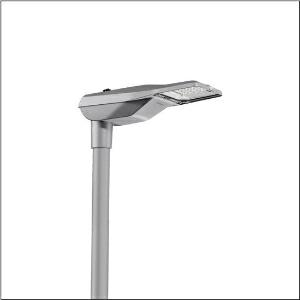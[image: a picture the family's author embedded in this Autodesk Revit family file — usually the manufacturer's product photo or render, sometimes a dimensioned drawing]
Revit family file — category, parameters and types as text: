
# Revit family: streetlight_sl_21_iq_micro___st1_0ab_5xe1m31v08cb_08ed
name_source: partatom
category: Lighting Fixtures
units: mm (PartAtom-declared; Revit-internal decimal feet)

## family parameters
Cut with Voids When Loaded = No
Host = Face
Light Source = No
Part Type = Normal
Room Calculation Point = No
Round Connector Dimension = Use Diameter
Shared = No

## types (1)
- --- (1 x LED, 2530 lm, 19.1 W, 3000K)
    Apparent Load = 19 VA
    CIE Flux Codes = 38 73 97 100 100
    Color Rendering = 70
    Color Temperature = 3000K
    Default Elevation = 1800 mm
    Description = Streetlight SL 21 iQ micro, mast luminaire, primary light control with lens, of PMMA, primary optical cover: cover, of toughened safety glass, transparent, light distribution: ST1.0aB, light emission: direct distribution, primary light characteristic: asymmetric, installation type: post-top, side-entry, LED, High Power LED, rated luminous flux: 2.530lm, luminous efficacy: 133lm/W, light colour: 730, colour temperature: 3000K, control: presetting dimming logarithmic, Street-Remote, Auto-Match, Temp-Guard, Lumen-Switch, Night-Set, Smart-Wire, Light-Fading, Desk-Remote (wireless, voltage-free reading and setting of iQ features in the workshop via application-optimized NFC function/RFID function), optimised constant luminous flux control (CLO 2.0), mains connection: 220..240V, AC, 50/60Hz, start of lifetime: 19W, end of service life: 20W, reduction: 9W, luminaire housing, of diecast aluminium, powder-coated, Siteco® metallic grey (DB 702S), corrosivity category C5 mid according to DIN EN ISO 12944, please order mast flange separately, inclination adjustable: 0°, 5°, 10°, 15°, sealing non-destructively replaceable, multi-level sealing system, length: 528mm, width: 235mm, height: 110mm, mast flange for spigot size: 42mm (side-entry): 5XC10008XM4, 60/48mm (side-entry/post-top): 5XC10108XM2, 76/60mm (side-entry/post-top): 5XC10108XM1, Smart Interface above, protection rating (complete): IP66, insulation class (complete): insulation class II (safety insulation), certification: CE, ENEC, ENEC+, VDE, impact resistance: IK09, permissible operating ambient temperature for outdoor applications: -40..+50°C, standard-compliant lighting for roads and squares, packaging unit: 1 piece

Light Distribution: ST1.0aB
    Height = 110 mm
    Lamp = 1 x LED
    Lamp Light Flux = 2530 lm
    Lamp Power = 19.1 W
    Lamp count = 1
    Length = 528 mm
    Luminous efficacy = 132 lm/W
    Manufacturer = Siteco
    ModVariant = No
    Model = 5XE1M31V08CB
    Number of Poles = 1
    OnlyDefault = Yes
    Power Factor = 1
    Product Name = Streetlight SL 21 iQ micro | ST1.0aB
    Product group = mast luminaire | pylon top
    ProductGroupID = 6100
    Protection Class = Protection class II
    Protection Degree = IP 66
    RLX_Detail_Level = 1
    RLX_Emergency_Light_Flux = 0 lm
    RLX_Emergency_Type = 0
    RLX_Emergency_Type_DB = No
    RlxData = <blob elided: 98605 chars, md5=d77db040>
    Socket = socket
    Standby Power = 0 W
    System Light Flux = 2530 lm
    System Power = 19 W
    Type Comments = factory setting: luminous flux: 100 % | dim-lin: 254 | 387 mA
    Type Image = l_1277292.jpg
    URL = http://relux.com
    VarID = @adj_060989
    Voltage = 0 V
    Weight = 0.00 kg
    Width = 235 mm

## geometry (parser evidence)
native form markers: Blend x4, Sweep x13
no freeform markers — native parametric forms only
